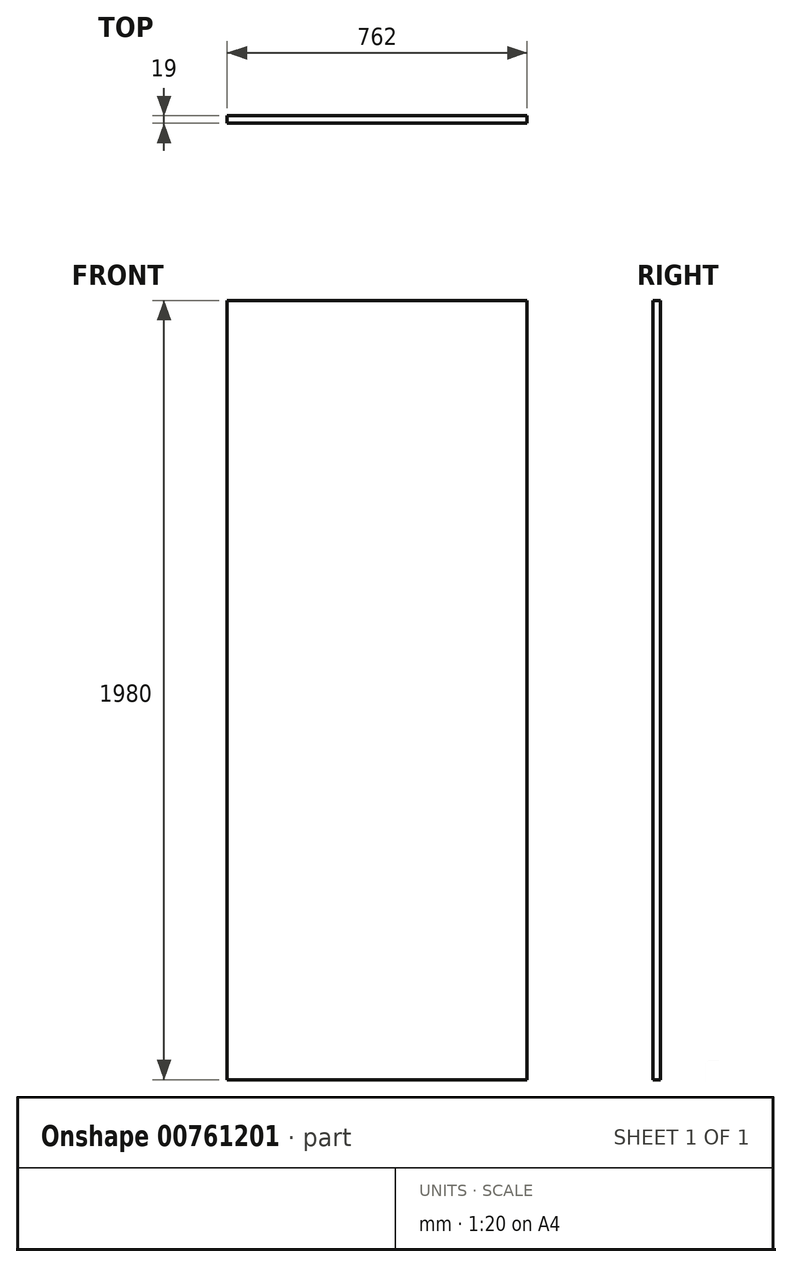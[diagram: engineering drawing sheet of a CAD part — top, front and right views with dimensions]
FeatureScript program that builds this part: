
annotation { "Feature Type Name" : "Feature", "Feature Type Description" : "" }
export const myFeature = defineFeature(function(context is Context, id is Id, definition is map)
    precondition{}
    {
        {
            var Q0;
            Q0=qCreatedBy(makeId("Front.planeOp"),FACE);
            var sketch = newSketch(context, id + "F0", { "sketchPlane" : qUnion([Q0])});
            skLineSegment(sketch, "E0.bottom", {"start": v(0, 0) * mm, "end": v(762, 0) * mm});
            skLineSegment(sketch, "E0.top", {"start": v(0, 1980) * mm, "end": v(762, 1980) * mm});
            skLineSegment(sketch, "E0.left", {"start": v(0, 0) * mm, "end": v(0, 1980) * mm});
            skLineSegment(sketch, "E0.right", {"start": v(762, 0) * mm, "end": v(762, 1980) * mm});
            skSolve(sketch);
        }
        {
            var Q0;
            Q0 = qSketchRegion(id + "F0", true);
            extrude(context, id + "F1", {"entities" : qUnion([Q0]), "depth" : 19 * mm, "offsetDistance" : 25 * mm});
        }
    });
